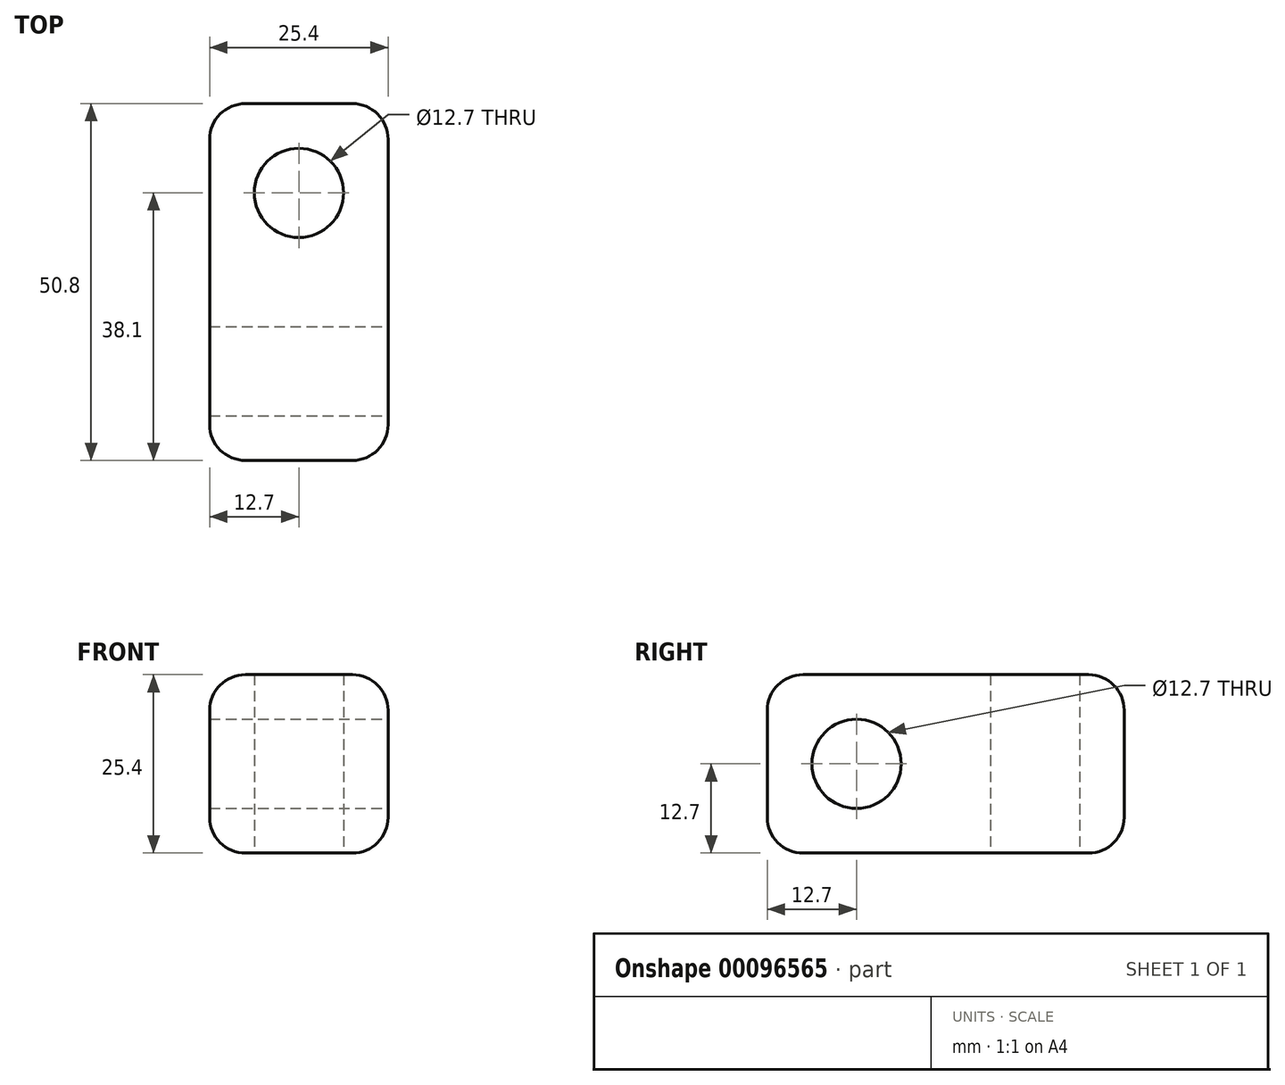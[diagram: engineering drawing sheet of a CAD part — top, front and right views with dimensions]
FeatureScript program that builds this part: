
annotation { "Feature Type Name" : "Feature", "Feature Type Description" : "" }
export const myFeature = defineFeature(function(context is Context, id is Id, definition is map)
    precondition{}
    {
        {
            var Q0;
            Q0=qCreatedBy(makeId("Top.planeOp"),FACE);
            var sketch = newSketch(context, id + "F0", { "sketchPlane" : qUnion([Q0])});
            skLineSegment(sketch, "E0.bottom", {"start": v(12.7, -25.4) * mm, "end": v(-12.7, -25.4) * mm});
            skLineSegment(sketch, "E0.top", {"start": v(12.7, 25.4) * mm, "end": v(-12.7, 25.4) * mm});
            skLineSegment(sketch, "E0.left", {"start": v(12.7, -25.4) * mm, "end": v(12.7, 25.4) * mm});
            skLineSegment(sketch, "E0.right", {"start": v(-12.7, -25.4) * mm, "end": v(-12.7, 25.4) * mm});
            skPoint(sketch, "E0.middle", {"position": v(0, 0) * mm});
            skLineSegment(sketch, "E1", {"start": v(0, 25.4) * mm, "end": v(0, -25.4) * mm, "construction": true});
            skLineSegment(sketch, "E2", {"start": v(-12.7, 0) * mm, "end": v(12.7, 0) * mm, "construction": true});
            skPoint(sketch, "E3", {"position": v(-12.7, 12.7) * mm});
            skPoint(sketch, "E4", {"position": v(-12.7, -12.47) * mm});
            skPoint(sketch, "E5", {"position": v(12.7, 12.7) * mm});
            skPoint(sketch, "E6", {"position": v(12.7, -11.83) * mm});
            skLineSegment(sketch, "E7", {"start": v(-12.7, 12.7) * mm, "end": v(12.7, 12.7) * mm, "construction": true});
            skCircle(sketch, "E8", {"center": v(0, 12.7) * mm, "radius": 6.35 * mm});
            skSolve(sketch);
        }
        {
            var Q0;
            Q0 = qSketchRegion(id + "F0", true);
            extrude(context, id + "F1", {"entities" : qUnion([Q0]), "depth" : 25.4 * mm, "symmetric" : true});
        }
        {
            var Q0;
            Q0=makeQuery(id+"F1.opExtrude","SWEPT_FACE",FACE,{"disambiguationData":[OSD([sQuery(id+"F0.wireOp",EDGE,"E0.right")])]});
            var sketch = newSketch(context, id + "F2", { "sketchPlane" : qUnion([Q0])});
            skLineSegment(sketch, "E9", {"start": v(25.4, 0) * mm, "end": v(0, 0) * mm});
            skCircle(sketch, "E10", {"center": v(12.7, 0) * mm, "radius": 6.35 * mm});
            skSolve(sketch);
        }
        {
            var Q0;
            Q0=sQuery(id+"F2.wireOp",VERTEX,"E10.center");
            var Q1;
            Q1=makeQuery(id+"F1.opExtrude","SWEPT_BODY",BODY,{"disambiguationData":[OSD([sQuery(id+"F0.wireOp",EDGE,"E0.bottom"),sQuery(id+"F0.wireOp",EDGE,"E0.top"),sQuery(id+"F0.wireOp",EDGE,"E0.left"),sQuery(id+"F0.wireOp",EDGE,"E0.right"),sQuery(id+"F0.wireOp",EDGE,"E8")])]});
            hole(context, id + "F3", {"style" : HoleStyle.SIMPLE, "endStyle" : HoleEndStyle.THROUGH, "holeDiameter" : 12.7 * mm, "locations" : qUnion([Q0]), "scope" : qUnion([Q1]), "isTappedThrough" : true, "startStyle" : HoleStartStyle.PART});
        }
        {
            var Q0;
            Q0=makeQuery(id+"F1.opExtrude","SWEPT_FACE",FACE,{"disambiguationData":[OSD([sQuery(id+"F0.wireOp",EDGE,"E0.bottom")])]});
            var Q1;
            Q1=makeQuery(id+"F1.opExtrude","SWEPT_FACE",FACE,{"disambiguationData":[OSD([sQuery(id+"F0.wireOp",EDGE,"E0.top")])]});
            var Q2;
            Q2=makeQuery(id+"F1.opExtrude","CAP_EDGE",EDGE,{"disambiguationData":[OSD([sQuery(id+"F0.wireOp",EDGE,"E0.right")])],"isStart":true});
            var Q3;
            Q3=makeQuery(id+"F1.opExtrude","CAP_EDGE",EDGE,{"disambiguationData":[OSD([sQuery(id+"F0.wireOp",EDGE,"E0.left")])],"isStart":true});
            var Q4;
            Q4=makeQuery(id+"F1.opExtrude","CAP_EDGE",EDGE,{"disambiguationData":[OSD([sQuery(id+"F0.wireOp",EDGE,"E0.left")])],"isStart":false});
            var Q5;
            Q5=makeQuery(id+"F1.opExtrude","CAP_EDGE",EDGE,{"disambiguationData":[OSD([sQuery(id+"F0.wireOp",EDGE,"E0.right")])],"isStart":false});
            fillet(context, id + "F4", {"entities" : qUnion([Q0, Q1, Q2, Q3, Q4, Q5]), "radius" : 5.08 * mm, "tangentPropagation" : true, "allowEdgeOverflow" : false});
        }
    });
